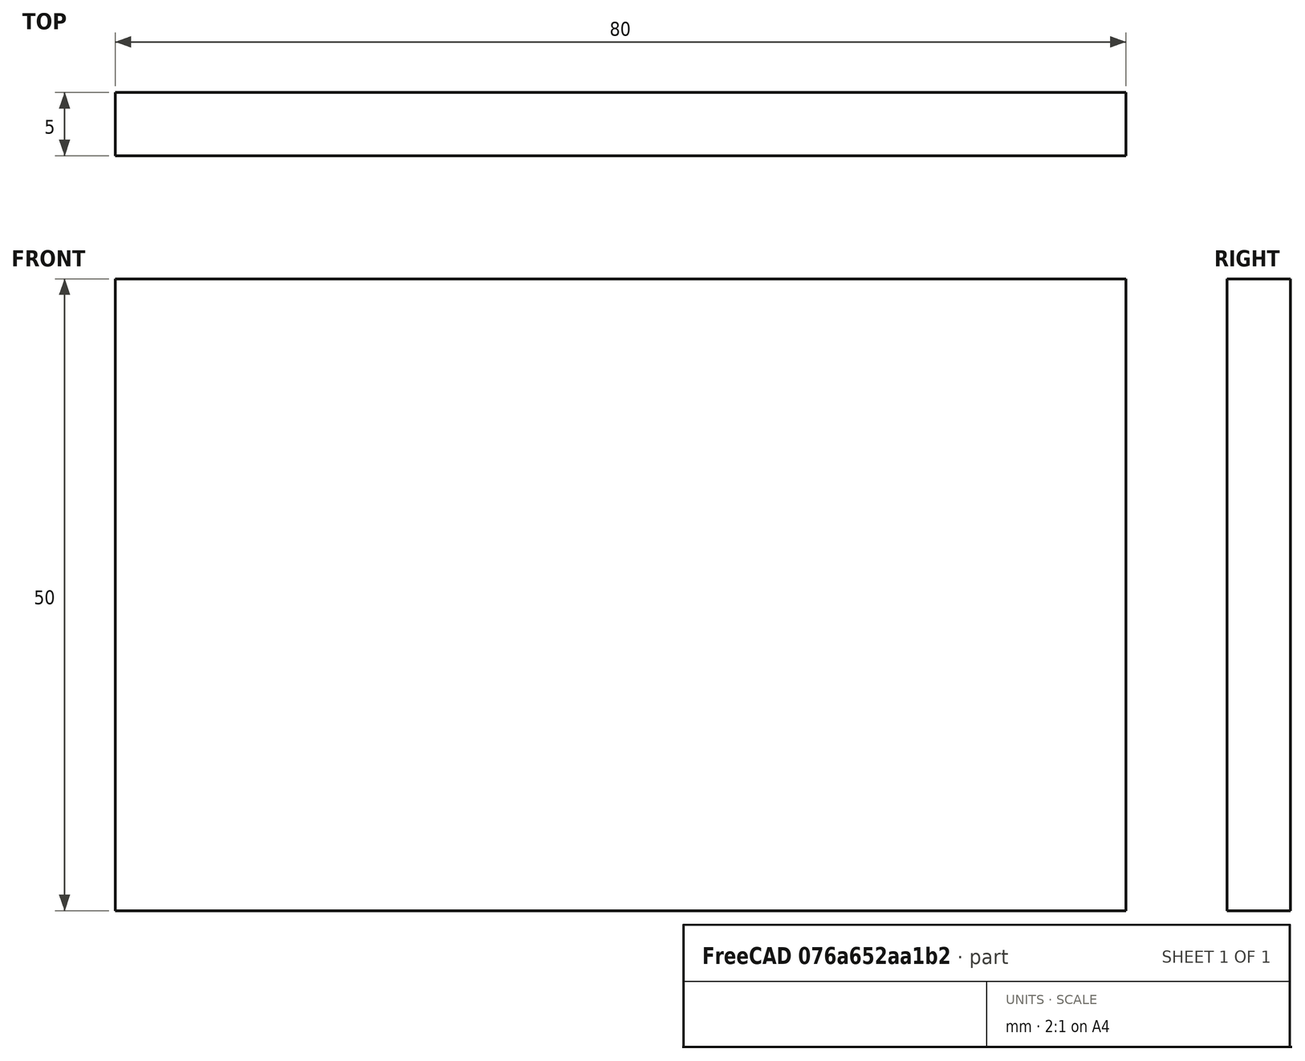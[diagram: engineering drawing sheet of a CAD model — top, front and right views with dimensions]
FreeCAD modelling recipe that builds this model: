
FCSTD DOCUMENT  (FreeCAD 0.15R4671 (Git))
Label: Flat Bar 80x5 EN10058 S235JR
License: All rights reserved
LicenseURL: http://en.wikipedia.org/wiki/All_rights_reserved
objects: Sketcher::SketchObject×1, Part::Extrusion×1
note: 2 computed .brp shape members not serialized (recipe doc carries the construction recipe); baked Part::Feature solids carry a one-line shape summary decoded from their .brp

FEATURE [Sketcher::SketchObject] Sketch
  sketch-geometry (4):
    g0: LineSegment StartX=-40 StartY=-2.5 StartZ=0 EndX=40 EndY=-2.5 EndZ=0
    g1: LineSegment StartX=40 StartY=-2.5 StartZ=0 EndX=40 EndY=2.5 EndZ=0
    g2: LineSegment StartX=40 StartY=2.5 StartZ=0 EndX=-40 EndY=2.5 EndZ=0
    g3: LineSegment StartX=-40 StartY=2.5 StartZ=0 EndX=-40 EndY=-2.5 EndZ=0
  constraints (12):
    c: Coincident(g0,g1)
    c: Coincident(g1,g2)
    c: Coincident(g2,g3)
    c: Coincident(g3,g0)
    c: Horizontal(g0)
    c: Horizontal(g2)
    c: Vertical(g1)
    c: Vertical(g3)
    c: Symmetric(g1,g2,g-2)
    c: Symmetric(g0,g1,g-1)
    c: DistanceY(g1) = 5
    c: DistanceX(g0) = 80
FEATURE [Part::Extrusion] Extrude  label="Flat Bar 80x5 EN10058 S235JR"
  Base = -> Sketch
  Dir = (0,0,50)
  Solid = true
